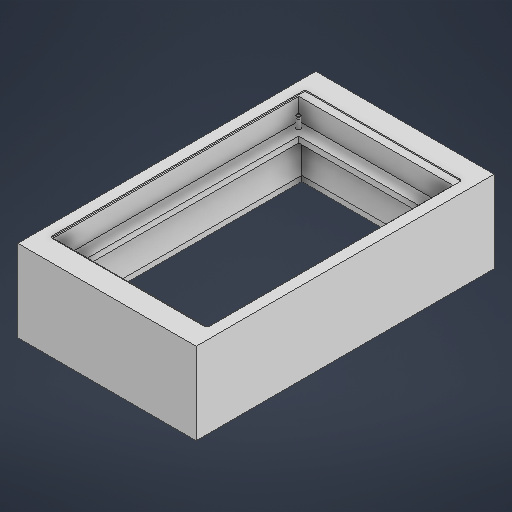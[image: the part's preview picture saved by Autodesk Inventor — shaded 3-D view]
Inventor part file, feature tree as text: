
AUTODESK INVENTOR PART (.ipt)
format: ipt  version: 2025.2 (Build 292293000, 293)  size: 332,800 bytes
history: native  units: in
note: dims shown in document units (in); Inventor stores cm internally (conversion verified against a paired STEP export)
features: extrude x10, sketch x10
ambient origin geometry x8: Origin, YZ Plane, XZ Plane, XY Plane, X Axis, Y Axis, Z Axis, Center Point
bodies: Solid1 (feature_tree)
feature tree (20):
  extrude  "Extrusion1"  Depth=10.9843in
  extrude  "Extrusion2"  Depth=5.7874in
  extrude  "Extrusion3"  Depth=0.0787in
  extrude  "Extrusion4"  Depth=0.0492in
  extrude  "Extrusion5"  Depth=5.689in
  extrude  "Extrusion8"  Depth=0.7874in TaperAngle=0.0deg
  extrude  "Extrusion9"  Depth=0.2362in
  extrude  "Extrusion10"  Depth=0.1575in
  extrude  "Extrusion11"  Depth=0.2264in
  extrude  "Extrusion12"  Depth=0.3937in
  sketch  "Sketch1"  dims[d0=6.5748in d1=10.9843in]
  sketch  "Sketch2"  dims[d2=1.0472in d3=0.0in d4=5.7874in]
  sketch  "Sketch3"  dims[d5=9.4094in d6=0.0787in]
  sketch  "Sketch4"  dims[d7=0.0433in d8=0.0in d9=0.0492in]
  sketch  "Sketch5"  dims[d10=0.0657in d11=5.689in]
  sketch  "Sketch8"  dims[d12=9.0591in d13=0.7874in d14=0.0in]
  sketch  "Sketch9"  dims[d15=0.1575in d16=0.2362in]
  sketch  "Sketch10"  dims[d17=0.2264in d18=0.1575in]
  sketch  "Sketch12"  dims[d19=0.2362in d20=0.2264in]
  sketch  "Sketch13"  dims[d21=0.1575in d22=0.2264in d23=0.2362in d24=0.1575in d25=0.2362in d26=0.2264in d27=0.4055in d28=0.0in d29=0.0984in d30=0.0984in d31=0.0984in d32=0.0984in d33=0.4055in d34=0.0in d35=0.2165in d36=0.0in d49=0.1378in d50=0.1378in d51=0.1378in d52=0.1378in d53=0.5433in d54=0.0in d55=4.7244in d56=7.874in d57=0.2283in d58=0.0in d59=1.5748in d60=0.0in d67=5.689in d68=9.0591in d69=0.1969in d70=0.1969in d71=9.4528in d72=0.1969in d73=0.1969in d74=9.4528in d75=0.3937in d76=0.0in d77=0.0984in d78=0.2362in d79=0.2362in d80=0.0984in d81=0.2362in d82=0.2362in d83=0.0984in d84=0.2362in d85=0.2362in d86=0.2362in d87=0.2362in d88=0.3937in d89=0.0in d47=0.0197in d48=0.0344in]
